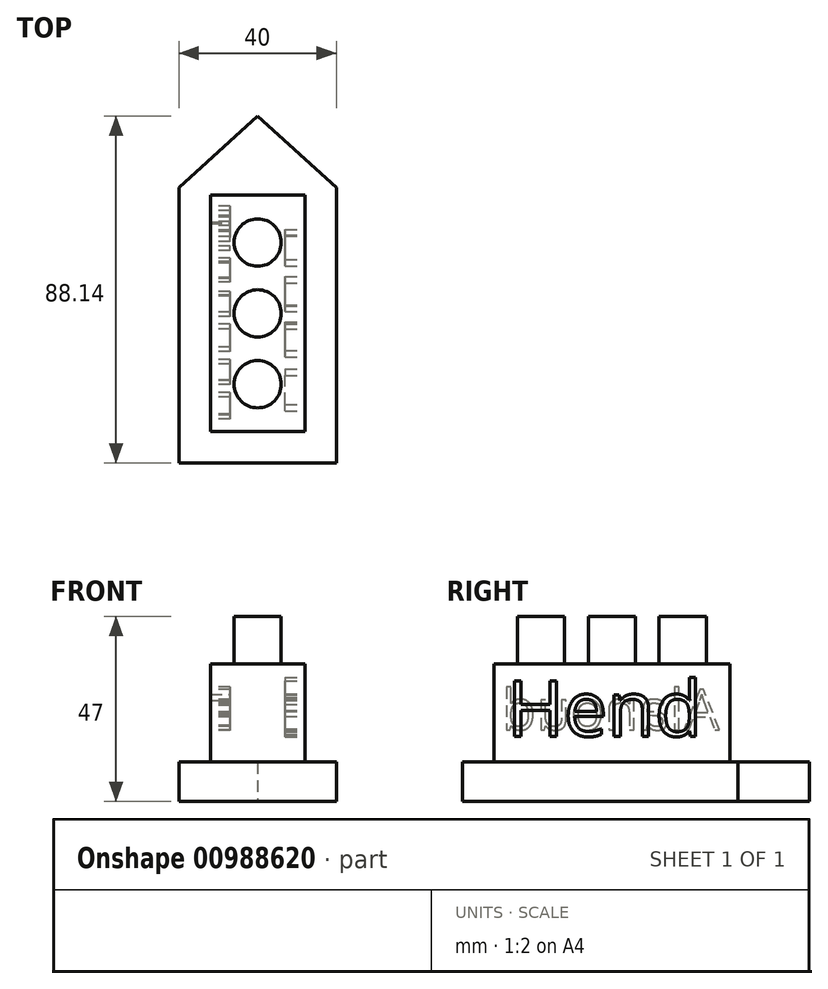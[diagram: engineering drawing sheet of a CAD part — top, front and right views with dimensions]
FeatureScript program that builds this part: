
annotation { "Feature Type Name" : "Feature", "Feature Type Description" : "" }
export const myFeature = defineFeature(function(context is Context, id is Id, definition is map)
    precondition{}
    {
        {
            var Q0;
            Q0=qCreatedBy(makeId("Top.planeOp"),FACE);
            var sketch = newSketch(context, id + "F0", { "sketchPlane" : qUnion([Q0])});
            skLineSegment(sketch, "E0", {"start": v(-36.68, 32.52) * mm, "end": v(-36.68, -37.48) * mm});
            skLineSegment(sketch, "E1", {"start": v(-36.68, -37.48) * mm, "end": v(3.32, -37.48) * mm});
            skLineSegment(sketch, "E2", {"start": v(3.32, -37.48) * mm, "end": v(3.32, 32.52) * mm});
            skLineSegment(sketch, "E3", {"start": v(-36.68, 32.52) * mm, "end": v(-16.68, 50.66) * mm});
            skLineSegment(sketch, "E4", {"start": v(3.32, 32.52) * mm, "end": v(-16.68, 50.66) * mm});
            skSolve(sketch);
        }
        {
            var Q0;
            Q0 = qSketchRegion(id + "F0", true);
            extrude(context, id + "F1", {"entities" : qUnion([Q0]), "depth" : 10 * mm, "offsetDistance" : 25 * mm});
        }
        {
            var Q0;
            Q0=makeQuery(id+"F1.opExtrude","CAP_FACE",FACE,{"disambiguationData":[OSD([sQuery(id+"F0.wireOp",EDGE,"E0"),sQuery(id+"F0.wireOp",EDGE,"E1"),sQuery(id+"F0.wireOp",EDGE,"E2"),sQuery(id+"F0.wireOp",EDGE,"E3"),sQuery(id+"F0.wireOp",EDGE,"E4")])],"isStart":false});
            var sketch = newSketch(context, id + "F2", { "sketchPlane" : qUnion([Q0])});
            skLineSegment(sketch, "E5", {"start": v(-28.68, 30.52) * mm, "end": v(-28.68, -29.48) * mm});
            skLineSegment(sketch, "E6", {"start": v(-28.68, -29.48) * mm, "end": v(-4.68, -29.48) * mm});
            skLineSegment(sketch, "E7", {"start": v(-4.68, -29.48) * mm, "end": v(-4.68, 30.52) * mm});
            skLineSegment(sketch, "E8", {"start": v(-4.68, 30.52) * mm, "end": v(-28.68, 30.52) * mm});
            skSolve(sketch);
        }
        {
            var Q0;
            Q0 = qSketchRegion(id + "F2", true);
            extrude(context, id + "F3", {"entities" : qUnion([Q0]), "operationType" : NewBodyOperationType.ADD, "depth" : 25 * mm, "offsetDistance" : 25 * mm});
        }
        {
            var Q0;
            Q0=makeQuery(id+"F3.opExtrude","CAP_FACE",FACE,{"disambiguationData":[OSD([sQuery(id+"F2.wireOp",EDGE,"E5"),sQuery(id+"F2.wireOp",EDGE,"E6"),sQuery(id+"F2.wireOp",EDGE,"E7"),sQuery(id+"F2.wireOp",EDGE,"E8")])],"isStart":false});
            var sketch = newSketch(context, id + "F4", { "sketchPlane" : qUnion([Q0])});
            skCircle(sketch, "E9", {"center": v(-16.68, 18.52) * mm, "radius": 6 * mm});
            skCircle(sketch, "E10", {"center": v(-16.68, 0.52) * mm, "radius": 6 * mm});
            skCircle(sketch, "E11", {"center": v(-16.68, -17.48) * mm, "radius": 6 * mm});
            skSolve(sketch);
        }
        {
            var Q0;
            Q0 = qSketchRegion(id + "F4", true);
            extrude(context, id + "F5", {"entities" : qUnion([Q0]), "operationType" : NewBodyOperationType.ADD, "depth" : 12 * mm, "offsetDistance" : 25 * mm});
        }
        {
            var Q0;
            Q0=makeQuery(id+"F3.opExtrude","SWEPT_FACE",FACE,{"disambiguationData":[OSD([sQuery(id+"F2.wireOp",EDGE,"E7")])]});
            var sketch = newSketch(context, id + "F6", { "sketchPlane" : qUnion([Q0])});
            skText(sketch, "E12", { "text": "Hend", "fontName": "OpenSans-Regular.ttf"});
            const initialGuessF6  = {"E12": [-0.0262, 0.01657, 1, 0, 0.01416]};
            skSetInitialGuess(sketch, initialGuessF6);
            skSolve(sketch);
        }
        {
            var Q0;
            Q0=makeQuery(id+"F3.opExtrude","SWEPT_FACE",FACE,{"disambiguationData":[OSD([sQuery(id+"F2.wireOp",EDGE,"E5")])]});
            var sketch = newSketch(context, id + "F7", { "sketchPlane" : qUnion([Q0])});
            skText(sketch, "E13", { "text": "Alanoud", "fontName": "OpenSans-Regular.ttf"});
            const initialGuessF7  = {"E13": [-0.02784, 0.01822, 1, 0, 0.01025]};
            skSetInitialGuess(sketch, initialGuessF7);
            skSolve(sketch);
        }
        {
            var Q0;
            Q0 = qSketchRegion(id + "F6", true);
            extrude(context, id + "F8", {"entities" : qUnion([Q0]), "operationType" : NewBodyOperationType.REMOVE, "oppositeDirection" : true, "depth" : 5 * mm, "offsetDistance" : 25 * mm});
        }
        {
            var Q0;
            Q0 = qSketchRegion(id + "F7", true);
            extrude(context, id + "F9", {"entities" : qUnion([Q0]), "operationType" : NewBodyOperationType.REMOVE, "oppositeDirection" : true, "depth" : 5 * mm, "offsetDistance" : 25 * mm});
        }
    });
